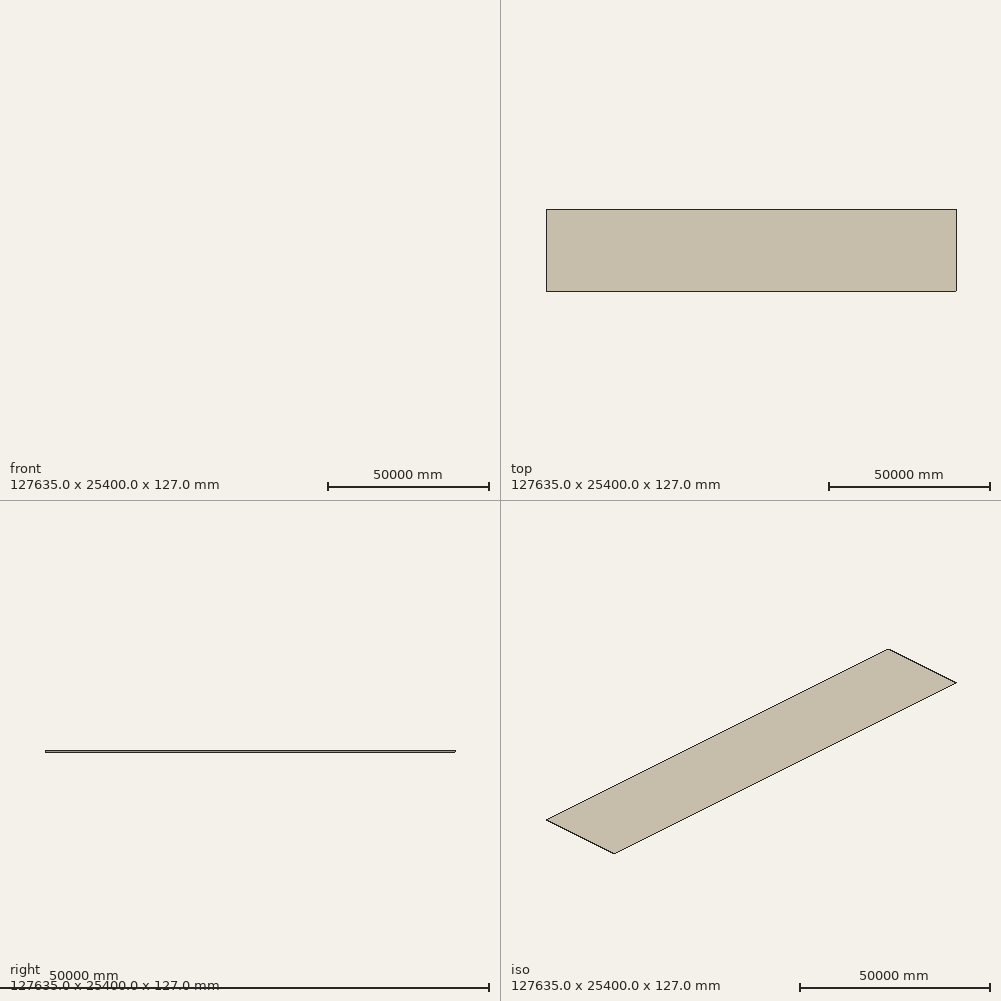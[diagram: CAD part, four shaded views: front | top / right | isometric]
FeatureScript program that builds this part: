
annotation { "Feature Type Name" : "Feature", "Feature Type Description" : "" }
export const myFeature = defineFeature(function(context is Context, id is Id, definition is map)
    precondition{}
    {
        {
            var Q0;
            Q0=qCreatedBy(makeId("Top.planeOp"),FACE);
            var sketch = newSketch(context, id + "F0", { "sketchPlane" : qUnion([Q0])});
            skLineSegment(sketch, "E0.bottom", {"start": v(-28.24, -47) * mm, "end": v(127606.76, -47) * mm});
            skLineSegment(sketch, "E0.top", {"start": v(-28.24, 25353) * mm, "end": v(127606.76, 25353) * mm});
            skLineSegment(sketch, "E0.left", {"start": v(-28.24, -47) * mm, "end": v(-28.24, 25353) * mm});
            skLineSegment(sketch, "E0.right", {"start": v(127606.76, -47) * mm, "end": v(127606.76, 25353) * mm});
            skSolve(sketch);
        }
        {
            var Q0;
            Q0 = qSketchRegion(id + "F0", true);
            var Q1;
            Q1=makeQuery(id+"F0.imprint","IMPRINT",FACE,{"disambiguationData":[TD([[makeQuery(id+"F0.imprint","IMPRINT",EDGE,{"derivedFrom":sQuery(id+"F0.wireOp",EDGE,"E0.bottom")}),1.0]])]});
            extrude(context, id + "F1", {"entities" : qUnion([Q0, Q1]), "depth" : 25.4 * mm});
        }
        {
            var Q0;
            Q0=makeQuery(id+"F1.opExtrude","CAP_FACE",FACE,{"disambiguationData":[OSD([sQuery(id+"F0.wireOp",EDGE,"E0.bottom"),sQuery(id+"F0.wireOp",EDGE,"E0.top"),sQuery(id+"F0.wireOp",EDGE,"E0.left"),sQuery(id+"F0.wireOp",EDGE,"E0.right")])],"isStart":false});
            extrude(context, id + "F2", {"entities" : qUnion([Q0]), "operationType" : NewBodyOperationType.ADD, "depth" : 25.4 * mm});
        }
        {
            var Q0;
            Q0=makeQuery(id+"F2.opExtrude","CAP_FACE",FACE,{"disambiguationData":[OSD([sQuery(id+"F0.wireOp",EDGE,"E0.bottom"),sQuery(id+"F0.wireOp",EDGE,"E0.top"),sQuery(id+"F0.wireOp",EDGE,"E0.left"),sQuery(id+"F0.wireOp",EDGE,"E0.right")])],"isStart":false});
            extrude(context, id + "F3", {"entities" : qUnion([Q0]), "operationType" : NewBodyOperationType.ADD, "depth" : 76.2 * mm});
        }
    });
